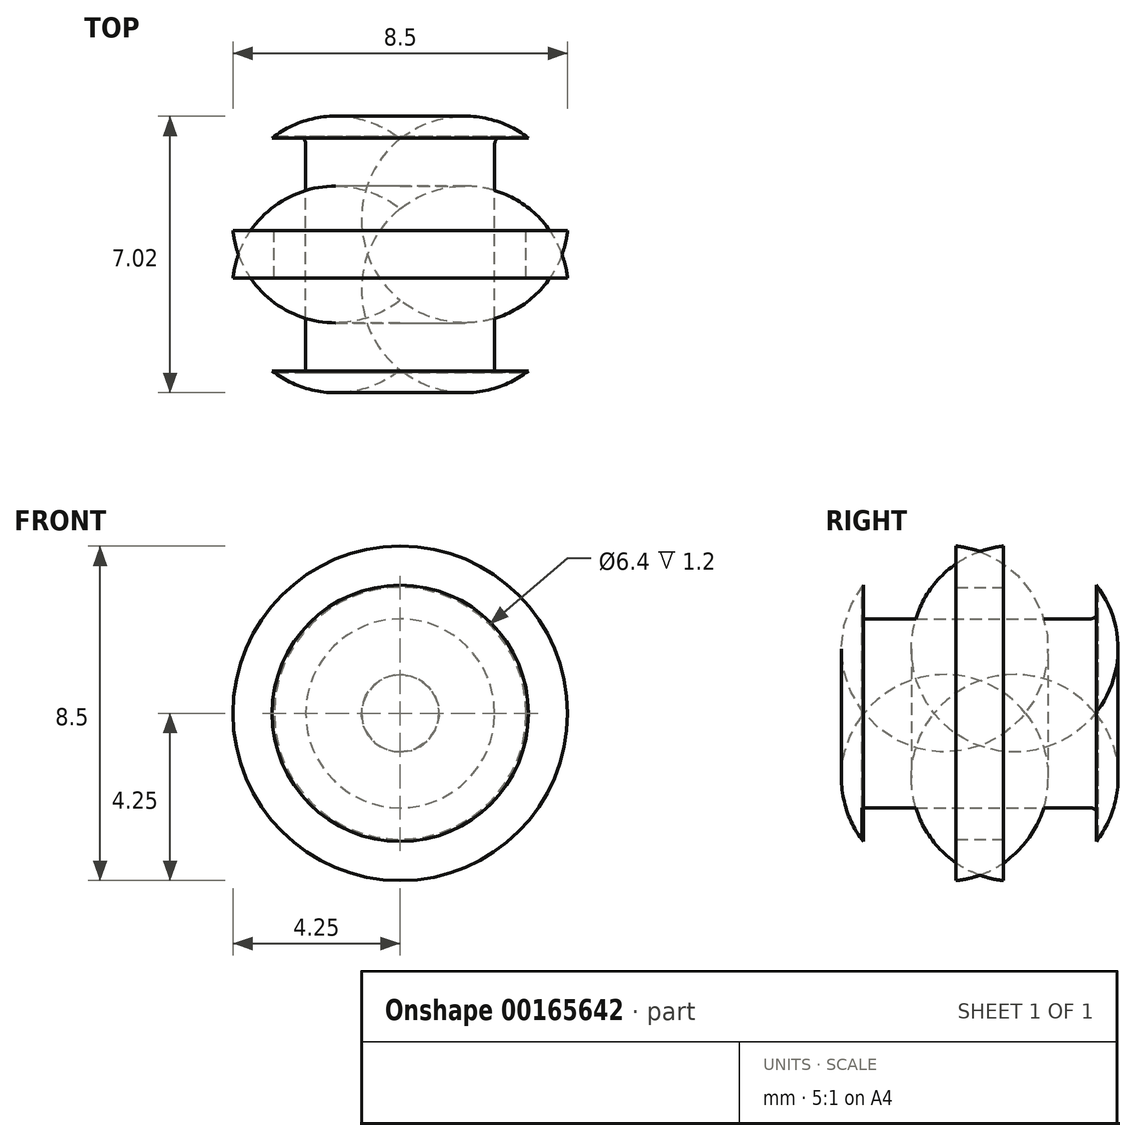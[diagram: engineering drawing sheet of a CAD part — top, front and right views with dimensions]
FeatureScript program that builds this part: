
annotation { "Feature Type Name" : "Feature", "Feature Type Description" : "" }
export const myFeature = defineFeature(function(context is Context, id is Id, definition is map)
    precondition{}
    {
        {
            var Q0;
            Q0=qCreatedBy(makeId("Top.planeOp"),FACE);
            var sketch = newSketch(context, id + "F0", { "sketchPlane" : qUnion([Q0])});
            skLineSegment(sketch, "E0", {"start": v(0, 3) * mm, "end": v(-3.2, 3) * mm});
            skArc(sketch, "E1", {"start": v(-3.2, 3) * mm, "mid": v(-4.05, 1.94) * mm, "end": v(-4.25, 0.6) * mm});
            skLineSegment(sketch, "E2", {"start": v(-4.25, 0.6) * mm, "end": v(-3.2, 0.6) * mm});
            skLineSegment(sketch, "E3", {"start": v(-3.2, 0.6) * mm, "end": v(-3.2, 0) * mm});
            skLineSegment(sketch, "E4", {"start": v(-3.2, 0) * mm, "end": v(0, 0) * mm});
            skLineSegment(sketch, "E5", {"start": v(0, 0) * mm, "end": v(0, 3) * mm});
            skLineSegment(sketch, "E6.MirrorCS", {"start": v(0, -3) * mm, "end": v(-3.2, -3) * mm});
            skArc(sketch, "E7.MirrorCS", {"start": v(-3.2, -3) * mm, "mid": v(-4.05, -1.94) * mm, "end": v(-4.25, -0.6) * mm});
            skLineSegment(sketch, "E8.MirrorCS", {"start": v(-4.25, -0.6) * mm, "end": v(-3.2, -0.6) * mm});
            skLineSegment(sketch, "E9.MirrorCS", {"start": v(-3.2, -0.6) * mm, "end": v(-3.2, 0) * mm});
            skLineSegment(sketch, "E10.MirrorCS", {"start": v(0, 0) * mm, "end": v(0, -3) * mm});
            skLineSegment(sketch, "E11", {"start": v(0, 5.31) * mm, "end": v(0, -4.56) * mm, "construction": true});
            skSolve(sketch);
        }
        {
            var Q0;
            Q0=makeQuery(id+"F0.imprint","IMPRINT",FACE,{"disambiguationData":[TD([[makeQuery(id+"F0.imprint","IMPRINT",EDGE,{"derivedFrom":sQuery(id+"F0.wireOp",EDGE,"E0")}),1.0]])]});
            var Q1;
            Q1=makeQuery(id+"F0.imprint","IMPRINT",FACE,{"disambiguationData":[TD([[makeQuery(id+"F0.imprint","IMPRINT",EDGE,{"derivedFrom":sQuery(id+"F0.wireOp",EDGE,"E4")}),-1.0]])]});
            var Q2;
            Q2=sQuery(id+"F0.wireOp",EDGE,"E11");
            revolve(context, id + "F1", {"surfaceOperationType" : NewSurfaceOperationType.NEW, "entities" : qUnion([Q0, Q1]), "axis" : qUnion([Q2]), "revolveType" : RevolveType.FULL});
        }
        {
            var Q0;
            Q0=makeQuery(id+"F1.opRevolve","SWEPT_FACE",FACE,{"disambiguationData":[OSD([sQuery(id+"F0.wireOp",EDGE,"E0")])]});
            var sketch = newSketch(context, id + "F2", { "sketchPlane" : qUnion([Q0])});
            skCircle(sketch, "E12", {"center": v(0, 0) * mm, "radius": 2.4 * mm});
            skSolve(sketch);
        }
        {
            var Q0;
            Q0=makeQuery(id+"F2.imprint","IMPRINT",FACE,{"disambiguationData":[TD([[makeQuery(id+"F2.imprint","IMPRINT",EDGE,{"derivedFrom":sQuery(id+"F2.wireOp",EDGE,"E12")}),1.0]])]});
            extrude(context, id + "F3", {"entities" : qUnion([Q0]), "operationType" : NewBodyOperationType.REMOVE, "endBound" : BoundingType.UP_TO_NEXT, "oppositeDirection" : true, "depth" : 25 * mm, "offsetDistance" : 25 * mm});
        }
        {
            var Q0;
            Q0=makeQuery(id+"F3.boolean.opBoolean","COPY",EDGE,{"derivedFrom":makeQuery(id+"F3.opExtrude","CAP_EDGE",EDGE,{"disambiguationData":[OSD([sQuery(id+"F2.wireOp",EDGE,"E12")])],"isStart":true})});
            var Q1;
            Q1=makeQuery(id+"F1.opRevolve","SWEPT_EDGE",EDGE,{"disambiguationData":[OSD([sQuery(id+"F0.wireOp",EDGE,"E0"),sQuery(id+"F0.wireOp",EDGE,"E1")])]});
            var Q2;
            Q2=makeQuery(id+"F3.boolean.opBoolean","COPY",EDGE,{"derivedFrom":makeQuery(id+"F3.opExtrude","TWEAK_EDGE",EDGE,{"derivedFrom":[makeQuery(id+"F1.opRevolve","SWEPT_FACE",FACE,{"disambiguationData":[OSD([sQuery(id+"F0.wireOp",EDGE,"E6.MirrorCS")])]}),makeQuery(id+"F2.imprint","IMPRINT",EDGE,{"derivedFrom":sQuery(id+"F2.wireOp",EDGE,"E12")})]})});
            var Q3;
            Q3=makeQuery(id+"F1.opRevolve","SWEPT_EDGE",EDGE,{"disambiguationData":[OSD([sQuery(id+"F0.wireOp",EDGE,"E6.MirrorCS"),sQuery(id+"F0.wireOp",EDGE,"E7.MirrorCS")])]});
            fillet(context, id + "F4", {"entities" : qUnion([Q0, Q1, Q2, Q3]), "radius" : 0.2 * mm, "tangentPropagation" : true});
        }
    });
